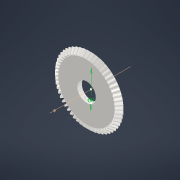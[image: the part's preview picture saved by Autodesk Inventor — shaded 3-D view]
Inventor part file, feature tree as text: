
AUTODESK INVENTOR PART (.ipt)
format: ipt  version: 2022 (Build 260153000, 153)  size: 875,520 bytes
history: native  units: mm
features: other x26, sketch x3, loft x2, pattern_circular x2, extrude x1, hole x1, reference x1
ambient origin geometry x6: Origin, XZ Plane, X Axis, Y Axis, Z Axis, Center Point
bodies: Solid1 (feature_tree)
feature tree (36):
  other  "Top Point"
  other  "Mesh Plane2"
  other  "Teeth Body"
  other  "Start Point"
  other  "Tooth Plane"
  other  "Start Sketch"
  other  "End Point"
  other  "3D Sketch Right"
  other  "End Plane Right"
  loft  "Loft Right"
  pattern_circular  "Circular Pattern Right"  [2 undecoded]
  other  "3D Sketch Left"
  other  "End Plane Left"
  loft  "Loft Left"
  pattern_circular  "Circular Pattern Left"  [2 undecoded]
  other  "Fix Body"
  extrude  "Extrusion1"  Depth=2.6mm
  hole  "Hole1"  [1 undecoded]
  other  "Mesh Plane"
  other  "Top Plane"
  other  "Teeth Body Sketch"
  other  "End Plane"
  other  "End Sketch"
  other  "Helical Curve Left"
  other  "End Sketch Left"
  other  "Body Sketch"
  sketch  "Sketch6"  dims[d0=108.0mm d1=104.515427mm]
  other  "Srf1"
  other  "Helical Curve Right"
  other  "End Sketch Right"
  sketch  "Sketch8"  dims[d2=110.903811mm]
  sketch  "Sketch10"  dims[d3=10.0mm d4=55.624511mm d5=90.0deg d7=26.134569mm d8=26.031741mm d9=65.120058mm d11=10.22mm d12=22.73284mm d15=22.643397mm d16=56.643899mm d17=0.0mm d18=90.0deg d19=0.0mm d20=90.0deg d21=540.0mm d22=360.0deg d26=670.288624mm d27=7.419236mm d28=108.0mm d29=-7.583777mm d30=22.73284mm d31=22.643397mm d32=56.643899mm d35=0.0mm d37=0.0mm d39=0.0mm d40=90.0deg d41=540.0mm d42=360.0deg d46=90.0deg d47=90.0deg d48=0.0mm d49=0.0mm d50=90.0deg d51=0.581776mm d52=0.0mm d53=0.0mm d54=0.0mm d56=35.128648mm d57=77.705013mm d58=71.457013mm d59=67.59077mm d60=62.156022mm d61=67.59077mm d62=62.156022mm d65=670.288624mm d66=31.5mm d67=108.0mm d68=-7.583777mm d69=7.419236mm d70=22.643397mm d71=56.643899mm d72=22.73284mm d73=62.156022mm d74=67.59077mm d75=0.0mm d77=0.0mm d79=0.0mm d80=90.0deg d81=540.0mm d82=360.0deg d84=10.0mm d85=20.0mm d86=20.0mm d87=10.0mm d88=0.0mm d89=0.0mm d90=90.0deg d91=90.0deg d92=90.0deg d93=90.0deg d95=0.0mm d96=0.0mm d99=30.0mm d100=3.4mm d101=6.0mm d102=6.0mm d103=2.6mm d104=14.3117mm d105=8.8mm d106=20.594885mm d107=0.75mm d108=20.594885mm d109=0.0625mm d110=0.75mm d111=0.375mm]
  reference  "Reference1"
  other  "Pitch Diameter"
  other  "SistemaDeElevación.iam"
  other  "Tuerca:1"
note: 5 required parameter values undecoded (feature->parameter linkage not recoverable at this tier; creation-order binding heuristic only, values carry confidence <= 0.55)
